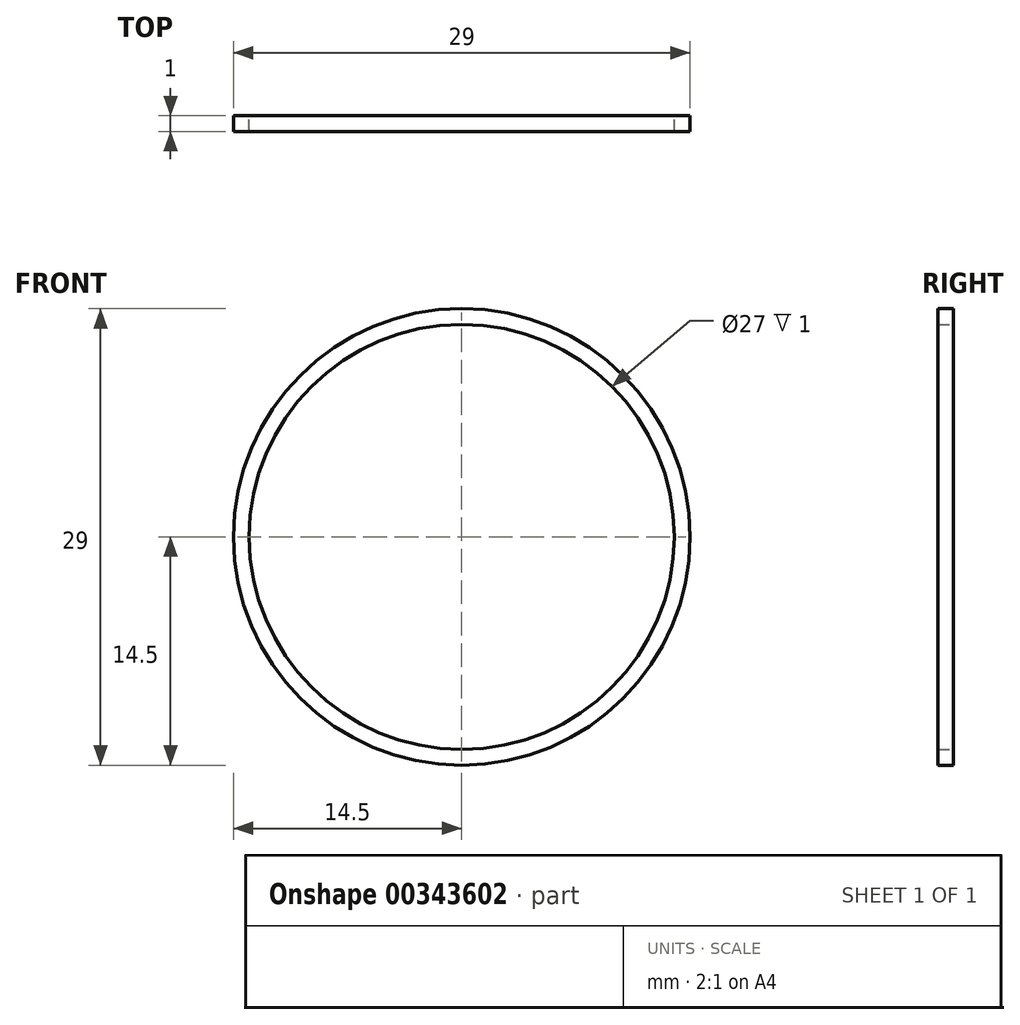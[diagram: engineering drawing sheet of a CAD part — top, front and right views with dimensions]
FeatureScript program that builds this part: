
annotation { "Feature Type Name" : "Feature", "Feature Type Description" : "" }
export const myFeature = defineFeature(function(context is Context, id is Id, definition is map)
    precondition{}
    {
        {
            var Q0;
            Q0=qCreatedBy(makeId("Front.planeOp"),FACE);
            var sketch = newSketch(context, id + "F0", { "sketchPlane" : qUnion([Q0])});
            skCircle(sketch, "E0", {"center": v(0, 0) * mm, "radius": 13.5 * mm});
            skCircle(sketch, "E1", {"center": v(0, 0) * mm, "radius": 14.5 * mm});
            skSolve(sketch);
        }
        {
            var Q0;
            Q0 = qSketchRegion(id + "F0", true);
            extrude(context, id + "F1", {"entities" : qUnion([Q0]), "depth" : 1 * mm});
        }
    });
